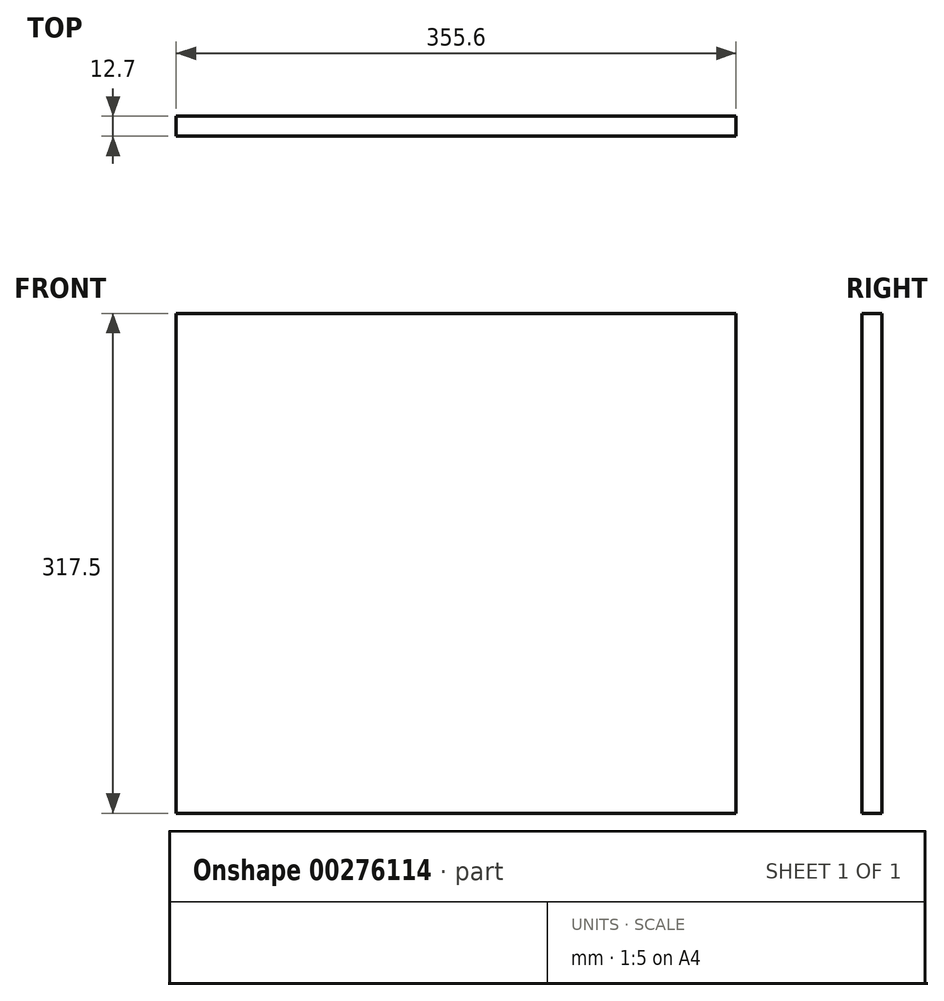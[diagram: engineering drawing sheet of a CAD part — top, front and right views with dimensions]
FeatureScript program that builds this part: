
annotation { "Feature Type Name" : "Feature", "Feature Type Description" : "" }
export const myFeature = defineFeature(function(context is Context, id is Id, definition is map)
    precondition{}
    {
        {
            var Q0;
            Q0=qCreatedBy(makeId("Front.planeOp"),FACE);
            var sketch = newSketch(context, id + "F0", { "sketchPlane" : qUnion([Q0])});
            skLineSegment(sketch, "E0.bottom", {"start": v(0, 0) * mm, "end": v(355.6, 0) * mm});
            skLineSegment(sketch, "E0.top", {"start": v(0, 317.5) * mm, "end": v(355.6, 317.5) * mm});
            skLineSegment(sketch, "E0.left", {"start": v(0, 0) * mm, "end": v(0, 317.5) * mm});
            skLineSegment(sketch, "E0.right", {"start": v(355.6, 0) * mm, "end": v(355.6, 317.5) * mm});
            skSolve(sketch);
        }
        {
            var Q0;
            Q0=makeQuery(id+"F0.imprint","IMPRINT",FACE,{"disambiguationData":[TD([[makeQuery(id+"F0.imprint","IMPRINT",EDGE,{"derivedFrom":sQuery(id+"F0.wireOp",EDGE,"E0.bottom")}),1.0]])]});
            extrude(context, id + "F1", {"entities" : qUnion([Q0]), "depth" : 12.7 * mm});
        }
    });
